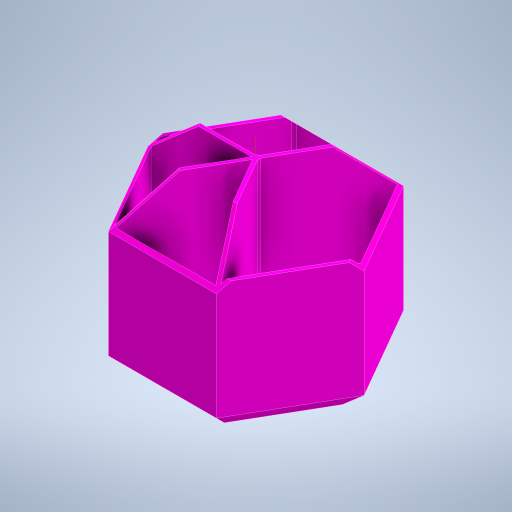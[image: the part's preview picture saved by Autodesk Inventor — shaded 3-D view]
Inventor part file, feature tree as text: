
AUTODESK INVENTOR PART (.ipt)
format: ipt  version: 2023 (Build 270158030, 158C)  size: 411,136 bytes
history: native  units: mm
features: projected_geometry x8, sketch x5, extrude x4, chamfer x4, other x1, pattern_circular x1
ambient origin geometry x8: Origin, YZ Plane, XZ Plane, XY Plane, X Axis, Y Axis, Z Axis, Center Point
bodies: Body1 (feature_tree)
feature tree (23):
  other  "pen-pot-body"
  extrude  "Extrusion1"  TaperAngle=60.0deg  [1 undecoded]
  extrude  "Extrusion2"  Depth=1.5mm
  extrude  "Extrusion3"  Depth=80.0mm
  pattern_circular  "Circular Pattern1"  Count=6 Angle=360.0deg
  chamfer  "Chamfer2"  Distance=70.0mm
  chamfer  "Chamfer1"  Distance=3.0mm
  chamfer  "Chamfer3"  Distance=8.0mm Angle=45.0deg
  chamfer  "Chamfer4"  Distance=7.0mm Angle=45.0deg
  extrude  "Extrusion4"  Depth=70.0mm TaperAngle=0.0deg
  sketch  "Sketch6"  dims[d31=19.0mm d32=2.0mm d33=45.0deg d34=15.0mm d35=0.0mm d36=32.0mm d37=24.0mm d38=17.5mm d41=20.0mm d42=240.0deg]
  sketch  "Sketch1"  dims[d5=60.0deg d6=60.0deg]
  sketch  "Sketch2"  dims[d7=0.75mm d8=1.5mm]
  projected_geometry  "Projected Loop1"
  sketch  "Sketch4"  dims[d9=1.3mm d10=80.0mm d11=60.0mm d13=360.0deg d16=70.0mm d17=0.0mm d18=3.0mm d19=0.0mm d20=8.0mm d21=2.0mm d22=45.0deg d23=7.0mm d24=2.0mm d25=45.0deg]
  projected_geometry  "Projected Loop3"
  sketch  "Sketch5"  dims[d26=19.0mm d27=2.0mm d28=45.0deg d29=70.0mm d30=0.0mm]
  projected_geometry  "Projected Loop4"
  projected_geometry  "Projected Loop5"
  projected_geometry  "Projected Loop6"
  projected_geometry  "Projected Loop7"
  projected_geometry  "Projected Loop8"
  projected_geometry  "Projected Loop9"
note: 1 required parameter value undecoded (feature->parameter linkage not recoverable at this tier; creation-order binding heuristic only, values carry confidence <= 0.55)
